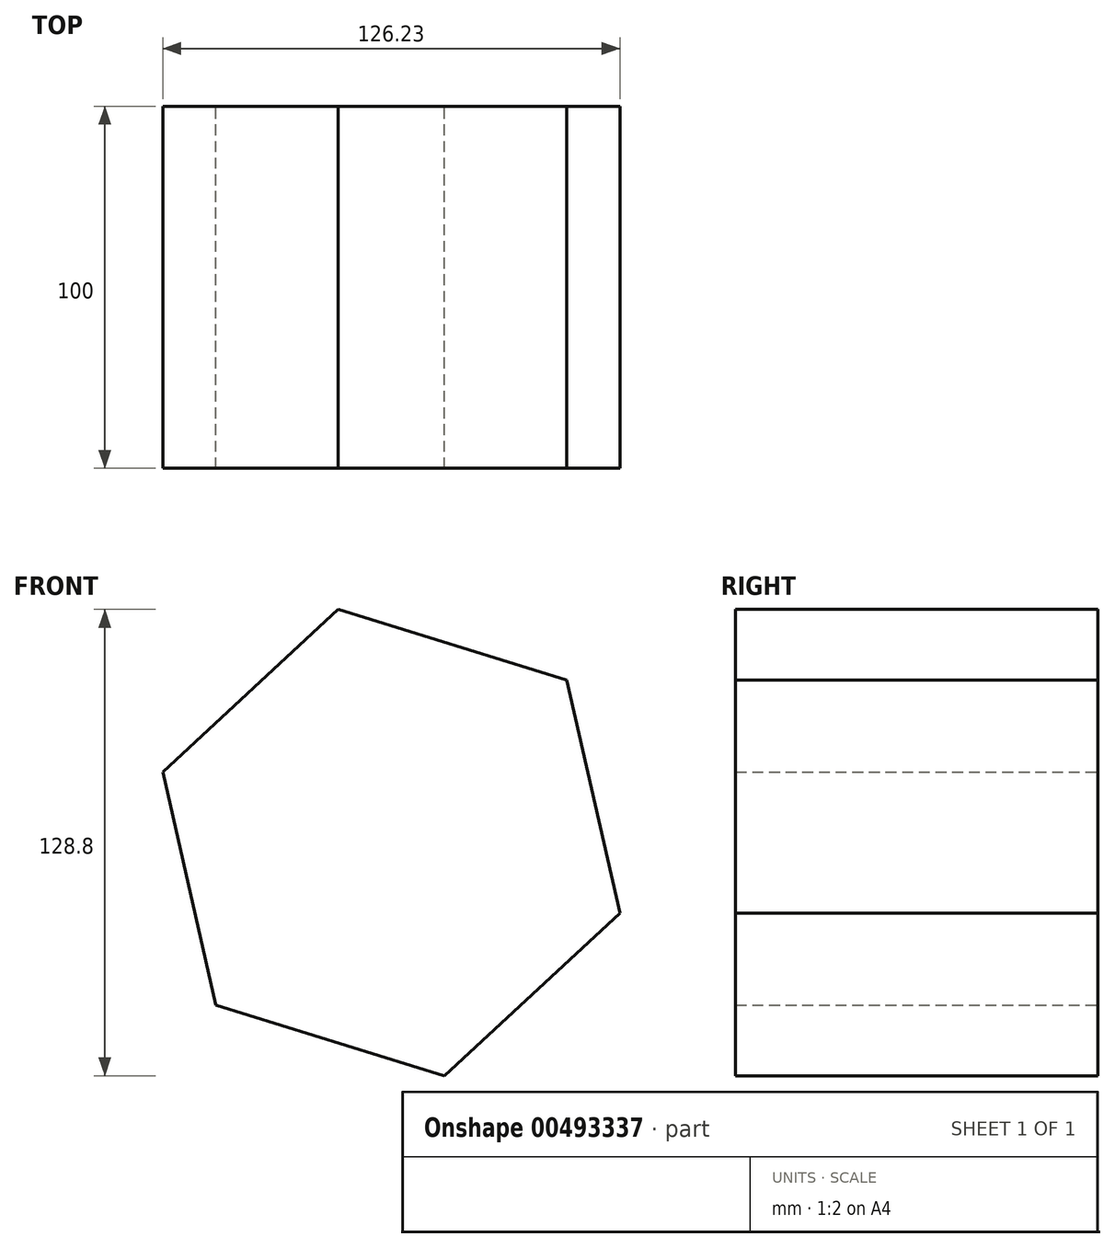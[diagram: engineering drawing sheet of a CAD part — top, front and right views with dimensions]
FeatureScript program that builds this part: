
annotation { "Feature Type Name" : "Feature", "Feature Type Description" : "" }
export const myFeature = defineFeature(function(context is Context, id is Id, definition is map)
    precondition{}
    {
        {
            var Q0;
            Q0=qCreatedBy(makeId("Front.planeOp"),FACE);
            var sketch = newSketch(context, id + "F0", { "sketchPlane" : qUnion([Q0])});
            skCircle(sketch, "E0.cCircle", {"center": v(-7.18, 0) * mm, "radius": 66.05 * mm, "construction": true});
            skLineSegment(sketch, "E0.0", {"start": v(-70.3, 19.47) * mm, "end": v(-21.88, 64.4) * mm});
            skLineSegment(sketch, "E0.1", {"start": v(-21.88, 64.4) * mm, "end": v(41.24, 44.92) * mm});
            skLineSegment(sketch, "E0.2", {"start": v(41.24, 44.92) * mm, "end": v(55.93, -19.47) * mm});
            skLineSegment(sketch, "E0.3", {"start": v(55.93, -19.47) * mm, "end": v(7.5, -64.4) * mm});
            skLineSegment(sketch, "E0.4", {"start": v(7.5, -64.4) * mm, "end": v(-55.6, -44.92) * mm});
            skLineSegment(sketch, "E0.5", {"start": v(-55.6, -44.92) * mm, "end": v(-70.3, 19.47) * mm});
            skSolve(sketch);
        }
        {
            var Q0;
            Q0=makeQuery(id+"F0.imprint","IMPRINT",FACE,{"disambiguationData":[TD([[makeQuery(id+"F0.imprint","IMPRINT",EDGE,{"derivedFrom":sQuery(id+"F0.wireOp",EDGE,"E0.0")}),-1.0]])]});
            extrude(context, id + "F1", {"entities" : qUnion([Q0]), "depth" : 100 * mm});
        }
    });
